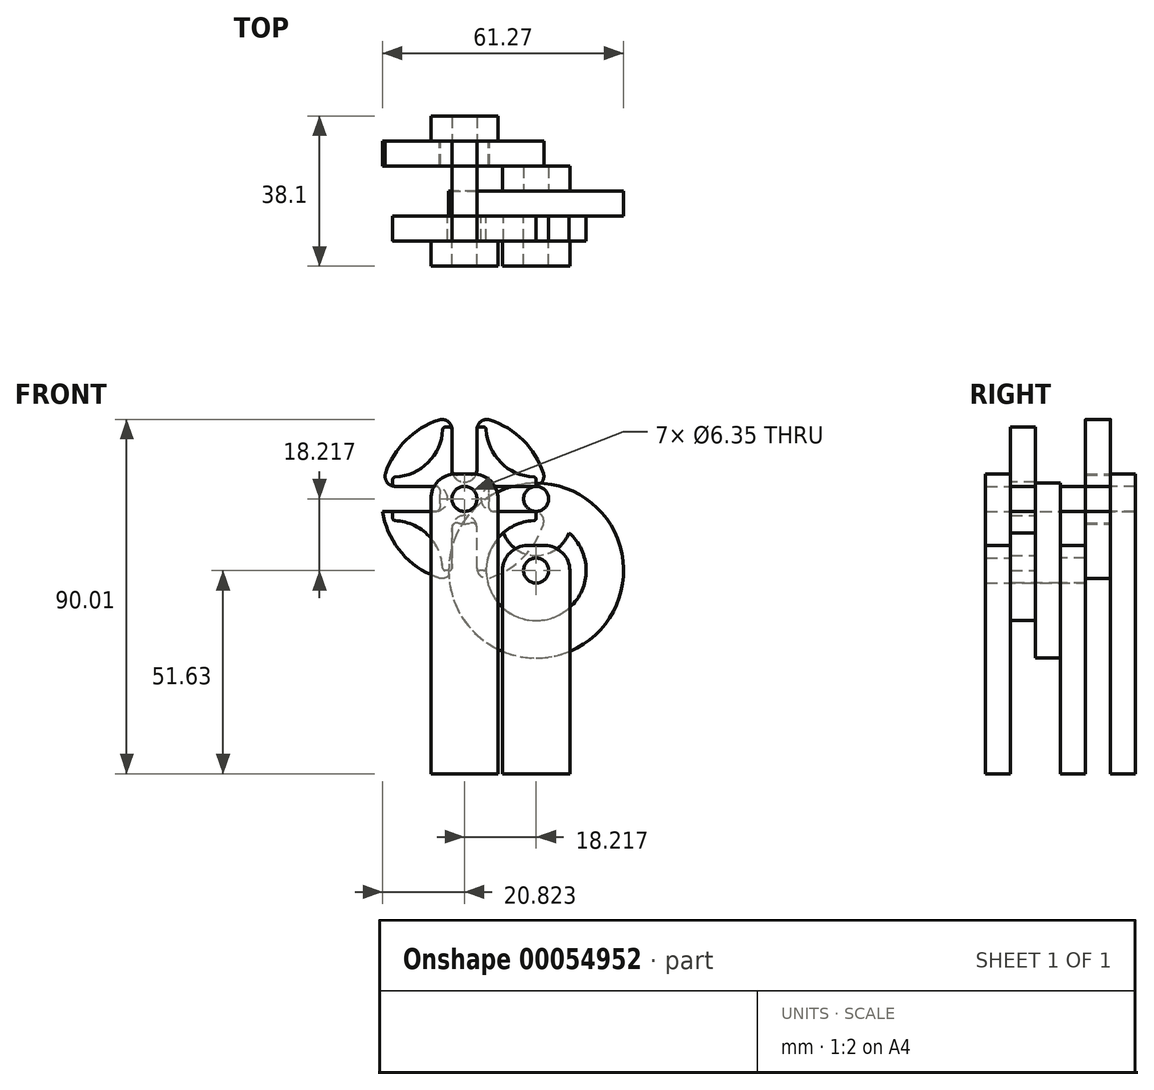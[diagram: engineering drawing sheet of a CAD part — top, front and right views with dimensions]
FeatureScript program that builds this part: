
annotation { "Feature Type Name" : "Feature", "Feature Type Description" : "" }
export const myFeature = defineFeature(function(context is Context, id is Id, definition is map)
    precondition{}
    {
        {
            var Q0;
            Q0=qCreatedBy(makeId("Front.planeOp"),FACE);
            var sketch = newSketch(context, id + "F0", { "sketchPlane" : qUnion([Q0])});
            skCircle(sketch, "E0", {"center": v(0, 0) * mm, "radius": 12.7 * mm});
            skCircle(sketch, "E1", {"center": v(0, 0) * mm, "radius": 22.23 * mm});
            skArc(sketch, "E2", {"start": v(-8.33, 9.59) * mm, "mid": v(0, 3.81) * mm, "end": v(8.33, 9.59) * mm});
            skCircle(sketch, "E3", {"center": v(0, 18.22) * mm, "radius": 3.18 * mm});
            skCircle(sketch, "E4", {"center": v(0, 0) * mm, "radius": 3.18 * mm});
            skSolve(sketch);
        }
        {
            var Q0;
            Q0=makeQuery(id+"F0.imprint","IMPRINT",FACE,{"disambiguationData":[TD([[makeQuery(id+"F0.imprint","IMPRINT",EDGE,{"derivedFrom":sQuery(id+"F0.wireOp",EDGE,"E1")}),1.0]])]});
            var Q1;
            Q1=makeQuery(id+"F0.imprint","IMPRINT",FACE,{"disambiguationData":[TD([[makeQuery(id+"F0.imprint","IMPRINT",EDGE,{"derivedFrom":sQuery(id+"F0.wireOp",EDGE,"E3")}),1.0]])]});
            var Q2;
            {var subQ0=sQuery(id+"F0.wireOp",EDGE,"E2");Q2=makeQuery(id+"F0.imprint","IMPRINT",FACE,{"disambiguationData":[TD([[makeQuery(id+"F0.imprint","IMPRINT",EDGE,{"derivedFrom":subQ0}),1.0]])]});}
            var Q3;
            {var subQ0=sQuery(id+"F0.wireOp",EDGE,"E2");Q3=makeQuery(id+"F0.imprint","IMPRINT",FACE,{"disambiguationData":[TD([[makeQuery(id+"F0.imprint","IMPRINT",EDGE,{"derivedFrom":subQ0}),-1.0]])]});}
            extrude(context, id + "F1", {"entities" : qUnion([Q0, Q1, Q2, Q3]), "oppositeDirection" : true, "depth" : 6.35 * mm});
        }
        {
            var Q0;
            Q0=makeQuery(id+"F0.imprint","IMPRINT",FACE,{"disambiguationData":[TD([[makeQuery(id+"F0.imprint","IMPRINT",EDGE,{"derivedFrom":sQuery(id+"F0.wireOp",EDGE,"E3")}),1.0]])]});
            var Q1;
            {var subQ0=sQuery(id+"F0.wireOp",EDGE,"E2");Q1=makeQuery(id+"F0.imprint","IMPRINT",FACE,{"disambiguationData":[TD([[makeQuery(id+"F0.imprint","IMPRINT",EDGE,{"derivedFrom":subQ0}),-1.0]])]});}
            extrude(context, id + "F2", {"entities" : qUnion([Q0, Q1]), "operationType" : NewBodyOperationType.ADD, "depth" : 6.35 * mm});
        }
        {
            var Q0;
            Q0=makeQuery(id+"F1.opExtrude","CAP_FACE",FACE,{"disambiguationData":[OSD([sQuery(id+"F0.wireOp",EDGE,"E1")])],"isStart":true});
            var sketch = newSketch(context, id + "F3", { "sketchPlane" : qUnion([Q0])});
            skArc(sketch, "E5", {"start": v(-12.7, 0) * mm, "mid": v(-8.98, 8.98) * mm, "end": v(0, 12.7) * mm});
            skLineSegment(sketch, "E6.bottom", {"start": v(0, 0) * mm, "end": v(-36.43, 0) * mm});
            skLineSegment(sketch, "E6.top", {"start": v(0, 36.43) * mm, "end": v(-36.43, 36.43) * mm});
            skLineSegment(sketch, "E6.left", {"start": v(0, 0) * mm, "end": v(0, 36.43) * mm});
            skLineSegment(sketch, "E6.right", {"start": v(-36.43, 0) * mm, "end": v(-36.43, 36.43) * mm});
            skLineSegment(sketch, "E7", {"start": v(-18.22, 36.43) * mm, "end": v(-18.22, 0) * mm, "construction": true});
            skLineSegment(sketch, "E8", {"start": v(-36.43, 18.22) * mm, "end": v(0, 18.22) * mm, "construction": true});
            skPoint(sketch, "E9", {"position": v(-18.22, 18.22) * mm});
            skCircle(sketch, "E10", {"center": v(-18.22, 18.22) * mm, "radius": 3.18 * mm});
            skLineSegment(sketch, "E11.bottom", {"start": v(0, 21.4) * mm, "end": v(-13.97, 21.4) * mm});
            skLineSegment(sketch, "E11.top", {"start": v(0, 15.04) * mm, "end": v(-13.97, 15.04) * mm});
            skLineSegment(sketch, "E11.left", {"start": v(0, 15.04) * mm, "end": v(0, 21.4) * mm});
            skLineSegment(sketch, "E11.right", {"start": v(-13.97, 15.04) * mm, "end": v(-13.97, 21.4) * mm});
            skLineSegment(sketch, "E12.1.0", {"start": v(-15.04, 36.43) * mm, "end": v(-15.04, 22.46) * mm});
            skLineSegment(sketch, "E12.1.1", {"start": v(-15.04, 22.46) * mm, "end": v(-21.4, 22.46) * mm});
            skLineSegment(sketch, "E12.1.2", {"start": v(-21.4, 36.43) * mm, "end": v(-21.4, 22.46) * mm});
            skArc(sketch, "E12.1.3", {"start": v(0, 23.73) * mm, "mid": v(-8.98, 27.45) * mm, "end": v(-12.7, 36.43) * mm});
            skLineSegment(sketch, "E12.2.0", {"start": v(-36.43, 21.4) * mm, "end": v(-22.46, 21.4) * mm});
            skLineSegment(sketch, "E12.2.1", {"start": v(-22.46, 21.4) * mm, "end": v(-22.46, 15.04) * mm});
            skLineSegment(sketch, "E12.2.2", {"start": v(-36.43, 15.04) * mm, "end": v(-22.46, 15.04) * mm});
            skArc(sketch, "E12.2.3", {"start": v(-23.73, 36.43) * mm, "mid": v(-27.45, 27.45) * mm, "end": v(-36.43, 23.73) * mm});
            skLineSegment(sketch, "E12.3.0", {"start": v(-21.4, 0) * mm, "end": v(-21.4, 13.97) * mm});
            skLineSegment(sketch, "E12.3.1", {"start": v(-21.4, 13.97) * mm, "end": v(-15.04, 13.97) * mm});
            skLineSegment(sketch, "E12.3.2", {"start": v(-15.04, 0) * mm, "end": v(-15.04, 13.97) * mm});
            skArc(sketch, "E12.3.3", {"start": v(-36.43, 12.7) * mm, "mid": v(-27.45, 8.98) * mm, "end": v(-23.73, 0) * mm});
            skLineSegment(sketch, "E13", {"start": v(0, 21.4) * mm, "end": v(0, 15.04) * mm});
            skLineSegment(sketch, "E14", {"start": v(-15.04, 36.43) * mm, "end": v(-21.4, 36.43) * mm});
            skLineSegment(sketch, "E15", {"start": v(-36.43, 21.4) * mm, "end": v(-36.43, 15.04) * mm});
            skLineSegment(sketch, "E16", {"start": v(-21.4, 0) * mm, "end": v(-15.04, 0) * mm});
            skSolve(sketch);
        }
        {
            var Q0;
            {var subQ5=sQuery(id+"F3.wireOp",EDGE,"E11.top");Q0=makeQuery(id+"F3.imprint","IMPRINT",FACE,{"disambiguationData":[TD([[makeQuery(id+"F3.imprint","IMPRINT",EDGE,{"derivedFrom":subQ5}),1.0]])]});}
            var Q1;
            {var subQ2=sQuery(id+"F3.wireOp",EDGE,"E12.1.0");Q1=makeQuery(id+"F3.imprint","IMPRINT",FACE,{"disambiguationData":[TD([[makeQuery(id+"F3.imprint","IMPRINT",EDGE,{"derivedFrom":subQ2}),1.0]])]});}
            var Q2;
            {var subQ0=sQuery(id+"F3.wireOp",EDGE,"E11.bottom");var subQ3=makeQuery(id+"F1.opExtrude","CAP_EDGE",EDGE,{"disambiguationData":[OSD([sQuery(id+"F0.wireOp",EDGE,"E1")])],"isStart":true});var subQ5=makeQuery(id+"F3.imprint","INTERSECT",VERTEX,{"derivedFrom":[subQ3,subQ0]});Q2=makeQuery(id+"F3.imprint","IMPRINT",FACE,{"disambiguationData":[TD([[makeQuery(id+"F3.imprint","IMPRINT",EDGE,{"disambiguationData":[TD([[subQ5,1.0]])],"derivedFrom":subQ3}),1.0]])]});}
            var Q3;
            {var subQ0=sQuery(id+"F3.wireOp",EDGE,"E12.3.0");var subQ3=makeQuery(id+"F1.opExtrude","CAP_EDGE",EDGE,{"disambiguationData":[OSD([sQuery(id+"F0.wireOp",EDGE,"E1")])],"isStart":true});var subQ5=makeQuery(id+"F3.imprint","INTERSECT",VERTEX,{"derivedFrom":[subQ3,subQ0]});Q3=makeQuery(id+"F3.imprint","IMPRINT",FACE,{"disambiguationData":[TD([[makeQuery(id+"F3.imprint","IMPRINT",EDGE,{"disambiguationData":[TD([[subQ5,1.0]])],"derivedFrom":subQ0}),1.0]])]});}
            extrude(context, id + "F4", {"entities" : qUnion([Q0, Q1, Q2, Q3]), "depth" : 6.35 * mm});
        }
        {
            var Q0;
            Q0=makeQuery(id+"F0.imprint","IMPRINT",FACE,{"disambiguationData":[TD([[makeQuery(id+"F0.imprint","IMPRINT",EDGE,{"derivedFrom":sQuery(id+"F0.wireOp",EDGE,"E4")}),1.0]])]});
            extrude(context, id + "F5", {"entities" : qUnion([Q0]), "depth" : 12.7 * mm, "hasSecondDirection" : true, "secondDirectionOppositeDirection" : true, "secondDirectionDepth" : 12.7 * mm});
        }
        {
            var Q0;
            Q0=makeQuery(id+"F3.imprint","IMPRINT",FACE,{"disambiguationData":[TD([[makeQuery(id+"F3.imprint","IMPRINT",EDGE,{"derivedFrom":sQuery(id+"F3.wireOp",EDGE,"E10")}),1.0]])]});
            var Q1;
            Q1=makeQuery(id+"F5.opExtrude","CAP_FACE",FACE,{"disambiguationData":[OSD([sQuery(id+"F0.wireOp",EDGE,"E4")])],"isStart":false});
            extrude(context, id + "F6", {"entities" : qUnion([Q0]), "endBoundEntityFace" : qUnion([Q1]), "depth" : 12.7 * mm, "hasSecondDirection" : true, "secondDirectionOppositeDirection" : true, "secondDirectionDepth" : 25.4 * mm});
        }
        {
            var Q0;
            Q0=makeQuery(id+"F4.opExtrude","SWEPT_EDGE",EDGE,{"disambiguationData":[OSD([sQuery(id+"F3.wireOp",EDGE,"E12.1.0"),sQuery(id+"F3.wireOp",EDGE,"E12.1.1")])]});
            var Q1;
            Q1=makeQuery(id+"F4.opExtrude","SWEPT_EDGE",EDGE,{"disambiguationData":[OSD([sQuery(id+"F3.wireOp",EDGE,"E12.1.1"),sQuery(id+"F3.wireOp",EDGE,"E12.1.2")])]});
            var Q2;
            Q2=makeQuery(id+"F4.opExtrude","SWEPT_EDGE",EDGE,{"disambiguationData":[OSD([sQuery(id+"F3.wireOp",EDGE,"E11.bottom"),sQuery(id+"F3.wireOp",EDGE,"E11.right")])]});
            var Q3;
            Q3=makeQuery(id+"F4.opExtrude","SWEPT_EDGE",EDGE,{"disambiguationData":[OSD([sQuery(id+"F3.wireOp",EDGE,"E11.top"),sQuery(id+"F3.wireOp",EDGE,"E11.right")])]});
            var Q4;
            Q4=makeQuery(id+"F4.opExtrude","SWEPT_EDGE",EDGE,{"disambiguationData":[OSD([sQuery(id+"F3.wireOp",EDGE,"E12.3.1"),sQuery(id+"F3.wireOp",EDGE,"E12.3.2")])]});
            var Q5;
            Q5=makeQuery(id+"F4.opExtrude","SWEPT_EDGE",EDGE,{"disambiguationData":[OSD([sQuery(id+"F3.wireOp",EDGE,"E12.3.0"),sQuery(id+"F3.wireOp",EDGE,"E12.3.1")])]});
            var Q6;
            Q6=makeQuery(id+"F4.opExtrude","SWEPT_EDGE",EDGE,{"disambiguationData":[OSD([sQuery(id+"F3.wireOp",EDGE,"E12.2.1"),sQuery(id+"F3.wireOp",EDGE,"E12.2.2")])]});
            var Q7;
            Q7=makeQuery(id+"F4.opExtrude","SWEPT_EDGE",EDGE,{"disambiguationData":[OSD([sQuery(id+"F3.wireOp",EDGE,"E12.2.0"),sQuery(id+"F3.wireOp",EDGE,"E12.2.1")])]});
            fillet(context, id + "F7", {"entities" : qUnion([Q0, Q1, Q2, Q3, Q4, Q5, Q6, Q7]), "radius" : 3.17 * mm, "tangentPropagation" : true, "allowEdgeOverflow" : false});
        }
        {
            var Q0;
            Q0=makeQuery(id+"F4.opExtrude","SWEPT_EDGE",EDGE,{"disambiguationData":[OSD([sQuery(id+"F3.wireOp",EDGE,"E6.top"),sQuery(id+"F3.wireOp",EDGE,"E12.1.3")])]});
            var Q1;
            Q1=makeQuery(id+"F4.opExtrude","SWEPT_EDGE",EDGE,{"disambiguationData":[OSD([sQuery(id+"F3.wireOp",EDGE,"E6.top"),sQuery(id+"F3.wireOp",EDGE,"E12.1.0"),sQuery(id+"F3.wireOp",EDGE,"E14")])]});
            var Q2;
            Q2=makeQuery(id+"F4.opExtrude","SWEPT_EDGE",EDGE,{"disambiguationData":[OSD([sQuery(id+"F3.wireOp",EDGE,"E6.top"),sQuery(id+"F3.wireOp",EDGE,"E12.1.2"),sQuery(id+"F3.wireOp",EDGE,"E14")])]});
            var Q3;
            Q3=makeQuery(id+"F4.opExtrude","SWEPT_EDGE",EDGE,{"disambiguationData":[OSD([sQuery(id+"F3.wireOp",EDGE,"E6.top"),sQuery(id+"F3.wireOp",EDGE,"E12.2.3")])]});
            var Q4;
            Q4=makeQuery(id+"F4.opExtrude","SWEPT_EDGE",EDGE,{"disambiguationData":[OSD([sQuery(id+"F3.wireOp",EDGE,"E6.right"),sQuery(id+"F3.wireOp",EDGE,"E12.2.3")])]});
            var Q5;
            Q5=makeQuery(id+"F4.opExtrude","SWEPT_EDGE",EDGE,{"disambiguationData":[OSD([sQuery(id+"F3.wireOp",EDGE,"E6.left"),sQuery(id+"F3.wireOp",EDGE,"E12.1.3")])]});
            var Q6;
            Q6=makeQuery(id+"F4.opExtrude","SWEPT_EDGE",EDGE,{"disambiguationData":[OSD([sQuery(id+"F0.wireOp",EDGE,"E3"),sQuery(id+"F3.wireOp",EDGE,"E6.left"),sQuery(id+"F3.wireOp",EDGE,"E11.bottom"),sQuery(id+"F3.wireOp",EDGE,"E13")])]});
            var Q7;
            Q7=makeQuery(id+"F4.opExtrude","SWEPT_EDGE",EDGE,{"disambiguationData":[OSD([sQuery(id+"F3.wireOp",EDGE,"E5"),sQuery(id+"F3.wireOp",EDGE,"E6.left")])]});
            var Q8;
            Q8=makeQuery(id+"F4.opExtrude","SWEPT_EDGE",EDGE,{"disambiguationData":[OSD([sQuery(id+"F3.wireOp",EDGE,"E6.right"),sQuery(id+"F3.wireOp",EDGE,"E12.2.2"),sQuery(id+"F3.wireOp",EDGE,"E15")])]});
            var Q9;
            Q9=makeQuery(id+"F4.opExtrude","SWEPT_EDGE",EDGE,{"disambiguationData":[OSD([sQuery(id+"F3.wireOp",EDGE,"E6.bottom"),sQuery(id+"F3.wireOp",EDGE,"E12.3.0"),sQuery(id+"F3.wireOp",EDGE,"E16")])]});
            var Q10;
            Q10=makeQuery(id+"F4.opExtrude","SWEPT_EDGE",EDGE,{"disambiguationData":[OSD([sQuery(id+"F3.wireOp",EDGE,"E6.right"),sQuery(id+"F3.wireOp",EDGE,"E12.2.0"),sQuery(id+"F3.wireOp",EDGE,"E15")])]});
            var Q11;
            Q11=makeQuery(id+"F4.opExtrude","SWEPT_EDGE",EDGE,{"disambiguationData":[OSD([sQuery(id+"F3.wireOp",EDGE,"E6.right"),sQuery(id+"F3.wireOp",EDGE,"E12.3.3")])]});
            var Q12;
            Q12=makeQuery(id+"F4.opExtrude","SWEPT_EDGE",EDGE,{"disambiguationData":[OSD([sQuery(id+"F3.wireOp",EDGE,"E6.bottom"),sQuery(id+"F3.wireOp",EDGE,"E12.3.3")])]});
            var Q13;
            Q13=makeQuery(id+"F4.opExtrude","SWEPT_EDGE",EDGE,{"disambiguationData":[OSD([sQuery(id+"F3.wireOp",EDGE,"E6.bottom"),sQuery(id+"F3.wireOp",EDGE,"E12.3.2"),sQuery(id+"F3.wireOp",EDGE,"E16")])]});
            var Q14;
            Q14=makeQuery(id+"F4.opExtrude","SWEPT_EDGE",EDGE,{"disambiguationData":[OSD([sQuery(id+"F0.wireOp",EDGE,"E0"),sQuery(id+"F3.wireOp",EDGE,"E5"),sQuery(id+"F3.wireOp",EDGE,"E6.bottom")])]});
            var Q15;
            Q15=makeQuery(id+"F4.opExtrude","SWEPT_EDGE",EDGE,{"disambiguationData":[OSD([sQuery(id+"F0.wireOp",EDGE,"E3"),sQuery(id+"F3.wireOp",EDGE,"E6.left"),sQuery(id+"F3.wireOp",EDGE,"E11.top"),sQuery(id+"F3.wireOp",EDGE,"E13")])]});
            fillet(context, id + "F8", {"entities" : qUnion([Q0, Q1, Q2, Q3, Q4, Q5, Q6, Q7, Q8, Q9, Q10, Q11, Q12, Q13, Q14, Q15]), "radius" : 0.64 * mm, "tangentPropagation" : true, "allowEdgeOverflow" : false});
        }
        {
            var Q0;
            Q0=makeQuery(id+"F2.opExtrude","CAP_FACE",FACE,{"disambiguationData":[OSD([sQuery(id+"F0.wireOp",EDGE,"E0"),sQuery(id+"F0.wireOp",EDGE,"E2"),sQuery(id+"F0.wireOp",EDGE,"E4")])],"isStart":false});
            var sketch = newSketch(context, id + "F9", { "sketchPlane" : qUnion([Q0])});
            skLineSegment(sketch, "E17.bottom", {"start": v(-8.55, 6.35) * mm, "end": v(8.55, 6.35) * mm});
            skLineSegment(sketch, "E17.left", {"start": v(-8.55, 6.35) * mm, "end": v(-8.55, -51.63) * mm});
            skLineSegment(sketch, "E17.right", {"start": v(8.55, 6.35) * mm, "end": v(8.55, -51.63) * mm});
            skLineSegment(sketch, "E18", {"start": v(0, -51.63) * mm, "end": v(0, 6.35) * mm, "construction": true});
            skCircle(sketch, "E19", {"center": v(0, 0) * mm, "radius": 3.18 * mm});
            skLineSegment(sketch, "E20", {"start": v(-8.55, -51.63) * mm, "end": v(8.55, -51.63) * mm});
            skLineSegment(sketch, "E21.bottom", {"start": v(-26.76, 24.57) * mm, "end": v(-9.67, 24.57) * mm});
            skLineSegment(sketch, "E21.top", {"start": v(-26.76, -51.63) * mm, "end": v(-9.67, -51.63) * mm});
            skLineSegment(sketch, "E21.left", {"start": v(-26.76, 24.57) * mm, "end": v(-26.76, -51.63) * mm});
            skLineSegment(sketch, "E21.right", {"start": v(-9.67, 24.57) * mm, "end": v(-9.67, -51.63) * mm});
            skLineSegment(sketch, "E22", {"start": v(-18.22, 24.57) * mm, "end": v(-18.22, -51.63) * mm, "construction": true});
            skCircle(sketch, "E23.0", {"center": v(-18.22, 18.22) * mm, "radius": 3.18 * mm});
            skSolve(sketch);
        }
        {
            var Q0;
            Q0 = qSketchRegion(id + "F9", true);
            extrude(context, id + "F10", {"entities" : qUnion([Q0]), "depth" : 6.35 * mm});
        }
        {
            var Q0;
            Q0=makeQuery(id+"F1.opExtrude","CAP_FACE",FACE,{"disambiguationData":[OSD([sQuery(id+"F0.wireOp",EDGE,"E1"),sQuery(id+"F0.wireOp",EDGE,"E4")])],"isStart":false});
            var sketch = newSketch(context, id + "F11", { "sketchPlane" : qUnion([Q0])});
            skLineSegment(sketch, "E24.0.0", {"start": v(8.55, 6.35) * mm, "end": v(-8.55, 6.35) * mm});
            skLineSegment(sketch, "E24.0.1", {"start": v(-8.55, 6.35) * mm, "end": v(-8.55, -51.63) * mm});
            skLineSegment(sketch, "E24.0.2", {"start": v(-8.55, -51.63) * mm, "end": v(8.55, -51.63) * mm});
            skLineSegment(sketch, "E24.0.3", {"start": v(8.55, -51.63) * mm, "end": v(8.55, 6.35) * mm});
            skCircle(sketch, "E25.0", {"center": v(0, 0) * mm, "radius": 3.18 * mm});
            skSolve(sketch);
        }
        {
            var Q0;
            Q0 = qSketchRegion(id + "F11", true);
            extrude(context, id + "F12", {"entities" : qUnion([Q0]), "depth" : 6.35 * mm});
        }
        {
            var Q0;
            Q0=makeQuery(id+"F12.opExtrude","CAP_FACE",FACE,{"disambiguationData":[OSD([sQuery(id+"F11.wireOp",EDGE,"E24.0.0"),sQuery(id+"F11.wireOp",EDGE,"E24.0.1"),sQuery(id+"F11.wireOp",EDGE,"E24.0.2"),sQuery(id+"F11.wireOp",EDGE,"E24.0.3"),sQuery(id+"F11.wireOp",EDGE,"E25.0")])],"isStart":false});
            var sketch = newSketch(context, id + "F13", { "sketchPlane" : qUnion([Q0])});
            skCircle(sketch, "E26.0", {"center": v(18.22, 18.22) * mm, "radius": 3.18 * mm});
            skCircle(sketch, "E27", {"center": v(18.22, 18.22) * mm, "radius": 27.42 * mm});
            skLineSegment(sketch, "E28.bottom", {"start": v(11.87, 44.89) * mm, "end": v(24.57, 44.89) * mm});
            skLineSegment(sketch, "E28.top", {"start": v(11.87, 33.08) * mm, "end": v(24.57, 33.08) * mm});
            skLineSegment(sketch, "E28.left", {"start": v(11.87, 44.89) * mm, "end": v(11.87, 33.08) * mm});
            skLineSegment(sketch, "E28.right", {"start": v(24.57, 44.89) * mm, "end": v(24.57, 33.08) * mm});
            skLineSegment(sketch, "E29.1.0", {"start": v(-8.45, 11.87) * mm, "end": v(-8.45, 24.57) * mm});
            skLineSegment(sketch, "E29.1.1", {"start": v(-8.45, 24.57) * mm, "end": v(3.35, 24.57) * mm});
            skLineSegment(sketch, "E29.1.2", {"start": v(-8.45, 11.87) * mm, "end": v(3.35, 11.87) * mm});
            skLineSegment(sketch, "E29.1.3", {"start": v(3.35, 11.87) * mm, "end": v(3.35, 24.57) * mm});
            skLineSegment(sketch, "E29.2.0", {"start": v(24.57, -8.45) * mm, "end": v(11.87, -8.45) * mm});
            skLineSegment(sketch, "E29.2.1", {"start": v(11.87, -8.45) * mm, "end": v(11.87, 3.35) * mm});
            skLineSegment(sketch, "E29.2.2", {"start": v(24.57, -8.45) * mm, "end": v(24.57, 3.35) * mm});
            skLineSegment(sketch, "E29.2.3", {"start": v(24.57, 3.35) * mm, "end": v(11.87, 3.35) * mm});
            skLineSegment(sketch, "E29.3.0", {"start": v(44.89, 24.57) * mm, "end": v(44.89, 11.87) * mm});
            skLineSegment(sketch, "E29.3.1", {"start": v(44.89, 11.87) * mm, "end": v(33.08, 11.87) * mm});
            skLineSegment(sketch, "E29.3.2", {"start": v(44.89, 24.57) * mm, "end": v(33.08, 24.57) * mm});
            skLineSegment(sketch, "E29.3.3", {"start": v(33.08, 24.57) * mm, "end": v(33.08, 11.87) * mm});
            skPoint(sketch, "E30", {"position": v(18.22, 33.08) * mm});
            skLineSegment(sketch, "E31.bottom", {"start": v(-5.28, 75.37) * mm, "end": v(41.71, 75.37) * mm});
            skLineSegment(sketch, "E31.top", {"start": v(-5.28, 44.89) * mm, "end": v(41.71, 44.89) * mm});
            skLineSegment(sketch, "E31.left", {"start": v(-8.45, 72.2) * mm, "end": v(-8.45, 48.06) * mm});
            skLineSegment(sketch, "E31.right", {"start": v(44.89, 72.2) * mm, "end": v(44.89, 48.06) * mm});
            skPoint(sketch, "E32", {"position": v(18.22, 44.89) * mm});
            skPoint(sketch, "E33.visualSharp", {"position": v(-8.45, 75.37) * mm});
            skArc(sketch, "E33.filletArc", {"start": v(-5.28, 75.37) * mm, "mid": v(-7.52, 74.44) * mm, "end": v(-8.45, 72.2) * mm});
            skPoint(sketch, "E34.visualSharp", {"position": v(44.89, 75.37) * mm});
            skArc(sketch, "E34.filletArc", {"start": v(44.89, 72.2) * mm, "mid": v(43.96, 74.44) * mm, "end": v(41.71, 75.37) * mm});
            skPoint(sketch, "E35.visualSharp", {"position": v(44.89, 44.89) * mm});
            skArc(sketch, "E35.filletArc", {"start": v(41.71, 44.89) * mm, "mid": v(43.96, 45.82) * mm, "end": v(44.89, 48.06) * mm});
            skPoint(sketch, "E36.visualSharp", {"position": v(-8.45, 44.89) * mm});
            skArc(sketch, "E36.filletArc", {"start": v(-8.45, 48.06) * mm, "mid": v(-7.52, 45.82) * mm, "end": v(-5.28, 44.89) * mm});
            skLineSegment(sketch, "E37.1.0", {"start": v(-35.76, 44.89) * mm, "end": v(-11.63, 44.89) * mm});
            skPoint(sketch, "E37.1.1", {"position": v(-8.45, 18.22) * mm});
            skLineSegment(sketch, "E37.1.2", {"start": v(-35.76, -8.45) * mm, "end": v(-11.63, -8.45) * mm});
            skPoint(sketch, "E37.1.3", {"position": v(-8.45, -8.45) * mm});
            skPoint(sketch, "E37.1.5", {"position": v(-38.93, 44.89) * mm});
            skPoint(sketch, "E37.1.6", {"position": v(-38.93, -8.45) * mm});
            skLineSegment(sketch, "E37.1.7", {"start": v(-38.93, -5.28) * mm, "end": v(-38.93, 41.71) * mm});
            skLineSegment(sketch, "E37.1.8", {"start": v(-8.45, -5.28) * mm, "end": v(-8.45, 41.71) * mm});
            skArc(sketch, "E37.1.10", {"start": v(-35.76, 44.89) * mm, "mid": v(-38, 43.96) * mm, "end": v(-38.93, 41.71) * mm});
            skArc(sketch, "E37.1.11", {"start": v(-8.45, 41.71) * mm, "mid": v(-9.38, 43.96) * mm, "end": v(-11.63, 44.89) * mm});
            skArc(sketch, "E37.1.12", {"start": v(-38.93, -5.28) * mm, "mid": v(-38, -7.52) * mm, "end": v(-35.76, -8.45) * mm});
            skArc(sketch, "E37.1.13", {"start": v(-11.63, -8.45) * mm, "mid": v(-9.38, -7.52) * mm, "end": v(-8.45, -5.28) * mm});
            skLineSegment(sketch, "E37.2.0", {"start": v(-8.45, -35.76) * mm, "end": v(-8.45, -11.63) * mm});
            skPoint(sketch, "E37.2.1", {"position": v(18.22, -8.45) * mm});
            skLineSegment(sketch, "E37.2.2", {"start": v(44.89, -35.76) * mm, "end": v(44.89, -11.63) * mm});
            skPoint(sketch, "E37.2.3", {"position": v(44.89, -8.45) * mm});
            skPoint(sketch, "E37.2.4", {"position": v(-8.45, -8.45) * mm});
            skPoint(sketch, "E37.2.5", {"position": v(-8.45, -38.93) * mm});
            skPoint(sketch, "E37.2.6", {"position": v(44.89, -38.93) * mm});
            skLineSegment(sketch, "E37.2.7", {"start": v(41.71, -38.93) * mm, "end": v(-5.28, -38.93) * mm});
            skLineSegment(sketch, "E37.2.8", {"start": v(41.71, -8.45) * mm, "end": v(-5.28, -8.45) * mm});
            skArc(sketch, "E37.2.10", {"start": v(-8.45, -35.76) * mm, "mid": v(-7.52, -38) * mm, "end": v(-5.28, -38.93) * mm});
            skArc(sketch, "E37.2.11", {"start": v(-5.28, -8.45) * mm, "mid": v(-7.52, -9.38) * mm, "end": v(-8.45, -11.63) * mm});
            skArc(sketch, "E37.2.12", {"start": v(41.71, -38.93) * mm, "mid": v(43.96, -38) * mm, "end": v(44.89, -35.76) * mm});
            skArc(sketch, "E37.2.13", {"start": v(44.89, -11.63) * mm, "mid": v(43.96, -9.38) * mm, "end": v(41.71, -8.45) * mm});
            skLineSegment(sketch, "E37.3.0", {"start": v(72.2, -8.45) * mm, "end": v(48.06, -8.45) * mm});
            skPoint(sketch, "E37.3.1", {"position": v(44.89, 18.22) * mm});
            skLineSegment(sketch, "E37.3.2", {"start": v(72.2, 44.89) * mm, "end": v(48.06, 44.89) * mm});
            skPoint(sketch, "E37.3.4", {"position": v(44.89, -8.45) * mm});
            skPoint(sketch, "E37.3.5", {"position": v(75.37, -8.45) * mm});
            skPoint(sketch, "E37.3.6", {"position": v(75.37, 44.89) * mm});
            skLineSegment(sketch, "E37.3.7", {"start": v(75.37, 41.71) * mm, "end": v(75.37, -5.28) * mm});
            skLineSegment(sketch, "E37.3.8", {"start": v(44.89, 41.71) * mm, "end": v(44.89, -5.28) * mm});
            skArc(sketch, "E37.3.10", {"start": v(72.2, -8.45) * mm, "mid": v(74.44, -7.52) * mm, "end": v(75.37, -5.28) * mm});
            skArc(sketch, "E37.3.11", {"start": v(44.89, -5.28) * mm, "mid": v(45.82, -7.52) * mm, "end": v(48.06, -8.45) * mm});
            skArc(sketch, "E37.3.12", {"start": v(75.37, 41.71) * mm, "mid": v(74.44, 43.96) * mm, "end": v(72.2, 44.89) * mm});
            skArc(sketch, "E37.3.13", {"start": v(48.06, 44.89) * mm, "mid": v(45.82, 43.96) * mm, "end": v(44.89, 41.71) * mm});
            skSolve(sketch);
        }
        {
            var Q0;
            Q0 = qSketchRegion(id + "F13", true);
            var Q1;
            {var subQ0=sQuery(id+"F13.wireOp",EDGE,"E28.top");var subQ1=sQuery(id+"F13.wireOp",EDGE,"E26.0");var subQ2=makeQuery(id+"F13.imprint","INTERSECT",VERTEX,{"derivedFrom":[subQ1,subQ0]});Q1=makeQuery(id+"F13.imprint","IMPRINT",FACE,{"disambiguationData":[TD([[makeQuery(id+"F13.imprint","IMPRINT",EDGE,{"disambiguationData":[TD([[subQ2,-1.0]])],"derivedFrom":subQ1}),-1.0]])]});}
            var Q2;
            {var subQ0=sQuery(id+"F13.wireOp",EDGE,"E28.top");var subQ1=sQuery(id+"F13.wireOp",EDGE,"E26.0");var subQ2=makeQuery(id+"F13.imprint","INTERSECT",VERTEX,{"derivedFrom":[subQ1,subQ0]});Q2=makeQuery(id+"F13.imprint","IMPRINT",FACE,{"disambiguationData":[TD([[makeQuery(id+"F13.imprint","IMPRINT",EDGE,{"disambiguationData":[TD([[subQ2,1.0]])],"derivedFrom":subQ1}),-1.0]])]});}
            var Q3;
            {var subQ0=sQuery(id+"F13.wireOp",EDGE,"E29.1.3");var subQ1=sQuery(id+"F13.wireOp",EDGE,"E26.0");var subQ2=makeQuery(id+"F13.imprint","INTERSECT",VERTEX,{"derivedFrom":[subQ1,subQ0]});Q3=makeQuery(id+"F13.imprint","IMPRINT",FACE,{"disambiguationData":[TD([[makeQuery(id+"F13.imprint","IMPRINT",EDGE,{"disambiguationData":[TD([[subQ2,-1.0]])],"derivedFrom":subQ1}),-1.0]])]});}
            var Q4;
            {var subQ0=sQuery(id+"F13.wireOp",EDGE,"E29.3.3");var subQ1=sQuery(id+"F13.wireOp",EDGE,"E26.0");var subQ2=makeQuery(id+"F13.imprint","INTERSECT",VERTEX,{"derivedFrom":[subQ1,subQ0]});Q4=makeQuery(id+"F13.imprint","IMPRINT",FACE,{"disambiguationData":[TD([[makeQuery(id+"F13.imprint","IMPRINT",EDGE,{"disambiguationData":[TD([[subQ2,1.0]])],"derivedFrom":subQ1}),-1.0]])]});}
            extrude(context, id + "F14", {"entities" : qUnion([Q0, Q1, Q2, Q3, Q4]), "depth" : 6.35 * mm});
        }
        {
            var Q0;
            Q0=makeQuery(id+"F14.opExtrude","CAP_FACE",FACE,{"disambiguationData":[OSD([sQuery(id+"F13.wireOp",EDGE,"E26.0"),sQuery(id+"F13.wireOp",EDGE,"E27"),sQuery(id+"F13.wireOp",EDGE,"E31.bottom"),sQuery(id+"F13.wireOp",EDGE,"E31.top"),sQuery(id+"F13.wireOp",EDGE,"E31.left"),sQuery(id+"F13.wireOp",EDGE,"E31.right"),sQuery(id+"F13.wireOp",EDGE,"E33.filletArc"),sQuery(id+"F13.wireOp",EDGE,"E34.filletArc"),sQuery(id+"F13.wireOp",EDGE,"E35.filletArc"),sQuery(id+"F13.wireOp",EDGE,"E36.filletArc"),sQuery(id+"F13.wireOp",EDGE,"E37.1.0"),sQuery(id+"F13.wireOp",EDGE,"E37.1.2"),sQuery(id+"F13.wireOp",EDGE,"E37.1.7"),sQuery(id+"F13.wireOp",EDGE,"E37.1.8"),sQuery(id+"F13.wireOp",EDGE,"E37.1.10"),sQuery(id+"F13.wireOp",EDGE,"E37.1.11"),sQuery(id+"F13.wireOp",EDGE,"E37.1.12"),sQuery(id+"F13.wireOp",EDGE,"E37.1.13"),sQuery(id+"F13.wireOp",EDGE,"E37.2.0"),sQuery(id+"F13.wireOp",EDGE,"E37.2.2"),sQuery(id+"F13.wireOp",EDGE,"E37.2.7"),sQuery(id+"F13.wireOp",EDGE,"E37.2.8"),sQuery(id+"F13.wireOp",EDGE,"E37.2.10"),sQuery(id+"F13.wireOp",EDGE,"E37.2.11"),sQuery(id+"F13.wireOp",EDGE,"E37.2.12"),sQuery(id+"F13.wireOp",EDGE,"E37.2.13"),sQuery(id+"F13.wireOp",EDGE,"E37.3.0"),sQuery(id+"F13.wireOp",EDGE,"E37.3.2"),sQuery(id+"F13.wireOp",EDGE,"E37.3.7"),sQuery(id+"F13.wireOp",EDGE,"E37.3.8"),sQuery(id+"F13.wireOp",EDGE,"E37.3.10"),sQuery(id+"F13.wireOp",EDGE,"E37.3.11"),sQuery(id+"F13.wireOp",EDGE,"E37.3.12"),sQuery(id+"F13.wireOp",EDGE,"E37.3.13")])],"isStart":false});
            var sketch = newSketch(context, id + "F15", { "sketchPlane" : qUnion([Q0])});
            skArc(sketch, "E38", {"start": v(21.4, 39.04) * mm, "mid": v(33.11, 33.11) * mm, "end": v(39.04, 21.4) * mm});
            skLineSegment(sketch, "E39", {"start": v(21.4, 39.04) * mm, "end": v(21.4, 21.4) * mm});
            skLineSegment(sketch, "E40", {"start": v(21.4, 21.4) * mm, "end": v(39.04, 21.4) * mm});
            skLineSegment(sketch, "E41.1.0", {"start": v(15.04, 21.4) * mm, "end": v(15.04, 39.04) * mm});
            skLineSegment(sketch, "E41.1.1", {"start": v(-2.6, 21.4) * mm, "end": v(15.04, 21.4) * mm});
            skArc(sketch, "E41.1.2", {"start": v(-2.6, 21.4) * mm, "mid": v(3.32, 33.11) * mm, "end": v(15.04, 39.04) * mm});
            skLineSegment(sketch, "E41.2.0", {"start": v(15.04, 15.04) * mm, "end": v(-2.6, 15.04) * mm});
            skLineSegment(sketch, "E41.2.1", {"start": v(15.04, -2.6) * mm, "end": v(15.04, 15.04) * mm});
            skArc(sketch, "E41.2.2", {"start": v(15.04, -2.6) * mm, "mid": v(3.32, 3.32) * mm, "end": v(-2.6, 15.04) * mm});
            skLineSegment(sketch, "E41.3.0", {"start": v(21.4, 15.04) * mm, "end": v(21.4, -2.6) * mm});
            skLineSegment(sketch, "E41.3.1", {"start": v(39.04, 15.04) * mm, "end": v(21.4, 15.04) * mm});
            skArc(sketch, "E41.3.2", {"start": v(39.04, 15.04) * mm, "mid": v(33.11, 3.32) * mm, "end": v(21.4, -2.6) * mm});
            skCircle(sketch, "E42", {"center": v(18.22, 18.22) * mm, "radius": 6.35 * mm});
            skSolve(sketch);
        }
        {
            var Q0;
            Q0=makeQuery(id+"F15.imprint","IMPRINT",FACE,{"disambiguationData":[TD([[makeQuery(id+"F15.imprint","IMPRINT",EDGE,{"derivedFrom":sQuery(id+"F15.wireOp",EDGE,"E38")}),-1.0]])]});
            var Q1;
            {var subQ0=sQuery(id+"F15.wireOp",EDGE,"E41.3.2");Q1=makeQuery(id+"F15.imprint","IMPRINT",FACE,{"disambiguationData":[TD([[makeQuery(id+"F15.imprint","IMPRINT",EDGE,{"derivedFrom":subQ0}),-1.0]])]});}
            var Q2;
            {var subQ0=sQuery(id+"F15.wireOp",EDGE,"E41.2.2");Q2=makeQuery(id+"F15.imprint","IMPRINT",FACE,{"disambiguationData":[TD([[makeQuery(id+"F15.imprint","IMPRINT",EDGE,{"derivedFrom":subQ0}),-1.0]])]});}
            var Q3;
            {var subQ0=sQuery(id+"F15.wireOp",EDGE,"E41.1.2");Q3=makeQuery(id+"F15.imprint","IMPRINT",FACE,{"disambiguationData":[TD([[makeQuery(id+"F15.imprint","IMPRINT",EDGE,{"derivedFrom":subQ0}),-1.0]])]});}
            extrude(context, id + "F16", {"entities" : qUnion([Q0, Q1, Q2, Q3]), "operationType" : NewBodyOperationType.REMOVE, "endBound" : BoundingType.UP_TO_NEXT, "oppositeDirection" : true, "depth" : 25.4 * mm});
        }
        {
            var Q0;
            Q0=makeQuery(id+"F14.opExtrude","SWEPT_EDGE",EDGE,{"disambiguationData":[OSD([sQuery(id+"F13.wireOp",EDGE,"E28.left"),sQuery(id+"F13.wireOp",EDGE,"E31.top")])]});
            var Q1;
            Q1=makeQuery(id+"F14.opExtrude","SWEPT_EDGE",EDGE,{"disambiguationData":[OSD([sQuery(id+"F13.wireOp",EDGE,"E28.right"),sQuery(id+"F13.wireOp",EDGE,"E31.top")])]});
            var Q2;
            Q2=makeQuery(id+"F14.opExtrude","SWEPT_EDGE",EDGE,{"disambiguationData":[OSD([sQuery(id+"F13.wireOp",EDGE,"E27"),sQuery(id+"F13.wireOp",EDGE,"E28.right")])]});
            var Q3;
            Q3=makeQuery(id+"F14.opExtrude","SWEPT_EDGE",EDGE,{"disambiguationData":[OSD([sQuery(id+"F13.wireOp",EDGE,"E27"),sQuery(id+"F13.wireOp",EDGE,"E28.left")])]});
            var Q4;
            Q4=makeQuery(id+"F14.opExtrude","SWEPT_EDGE",EDGE,{"disambiguationData":[OSD([sQuery(id+"F13.wireOp",EDGE,"E29.3.2"),sQuery(id+"F13.wireOp",EDGE,"E37.3.8"),sQuery(id+"F13.wireOp",EDGE,"E29.3.0")])]});
            var Q5;
            Q5=makeQuery(id+"F14.opExtrude","SWEPT_EDGE",EDGE,{"disambiguationData":[OSD([sQuery(id+"F13.wireOp",EDGE,"E27"),sQuery(id+"F13.wireOp",EDGE,"E29.3.2")])]});
            var Q6;
            Q6=makeQuery(id+"F14.opExtrude","SWEPT_EDGE",EDGE,{"disambiguationData":[OSD([sQuery(id+"F13.wireOp",EDGE,"E29.1.1"),sQuery(id+"F13.wireOp",EDGE,"E37.1.8"),sQuery(id+"F13.wireOp",EDGE,"E29.1.0")])]});
            var Q7;
            Q7=makeQuery(id+"F14.opExtrude","SWEPT_EDGE",EDGE,{"disambiguationData":[OSD([sQuery(id+"F13.wireOp",EDGE,"E27"),sQuery(id+"F13.wireOp",EDGE,"E29.1.1")])]});
            var Q8;
            Q8=makeQuery(id+"F14.opExtrude","SWEPT_EDGE",EDGE,{"disambiguationData":[OSD([sQuery(id+"F13.wireOp",EDGE,"E27"),sQuery(id+"F13.wireOp",EDGE,"E29.1.2")])]});
            var Q9;
            Q9=makeQuery(id+"F14.opExtrude","SWEPT_EDGE",EDGE,{"disambiguationData":[OSD([sQuery(id+"F13.wireOp",EDGE,"E29.1.2"),sQuery(id+"F13.wireOp",EDGE,"E37.1.8"),sQuery(id+"F13.wireOp",EDGE,"E29.1.0")])]});
            var Q10;
            Q10=makeQuery(id+"F14.opExtrude","SWEPT_EDGE",EDGE,{"disambiguationData":[OSD([sQuery(id+"F13.wireOp",EDGE,"E27"),sQuery(id+"F13.wireOp",EDGE,"E29.3.1")])]});
            var Q11;
            Q11=makeQuery(id+"F14.opExtrude","SWEPT_EDGE",EDGE,{"disambiguationData":[OSD([sQuery(id+"F13.wireOp",EDGE,"E29.3.1"),sQuery(id+"F13.wireOp",EDGE,"E37.3.8"),sQuery(id+"F13.wireOp",EDGE,"E29.3.0")])]});
            var Q12;
            Q12=makeQuery(id+"F14.opExtrude","SWEPT_EDGE",EDGE,{"disambiguationData":[OSD([sQuery(id+"F13.wireOp",EDGE,"E27"),sQuery(id+"F13.wireOp",EDGE,"E29.2.2")])]});
            var Q13;
            Q13=makeQuery(id+"F14.opExtrude","SWEPT_EDGE",EDGE,{"disambiguationData":[OSD([sQuery(id+"F13.wireOp",EDGE,"E29.2.2"),sQuery(id+"F13.wireOp",EDGE,"E37.2.8"),sQuery(id+"F13.wireOp",EDGE,"E29.2.0")])]});
            var Q14;
            Q14=makeQuery(id+"F14.opExtrude","SWEPT_EDGE",EDGE,{"disambiguationData":[OSD([sQuery(id+"F13.wireOp",EDGE,"E27"),sQuery(id+"F13.wireOp",EDGE,"E29.2.1")])]});
            var Q15;
            Q15=makeQuery(id+"F14.opExtrude","SWEPT_EDGE",EDGE,{"disambiguationData":[OSD([sQuery(id+"F13.wireOp",EDGE,"E29.2.1"),sQuery(id+"F13.wireOp",EDGE,"E37.2.8"),sQuery(id+"F13.wireOp",EDGE,"E29.2.0")])]});
            var Q16;
            Q16=makeQuery(id+"F16.boolean.opBoolean","COPY",EDGE,{"derivedFrom":makeQuery(id+"F16.opExtrude","SWEPT_EDGE",EDGE,{"disambiguationData":[OSD([sQuery(id+"F15.wireOp",EDGE,"E41.1.0"),sQuery(id+"F15.wireOp",EDGE,"E41.1.2")])]})});
            var Q17;
            Q17=makeQuery(id+"F16.boolean.opBoolean","COPY",EDGE,{"derivedFrom":makeQuery(id+"F16.opExtrude","SWEPT_EDGE",EDGE,{"disambiguationData":[OSD([sQuery(id+"F15.wireOp",EDGE,"E41.1.1"),sQuery(id+"F15.wireOp",EDGE,"E41.1.2")])]})});
            var Q18;
            Q18=makeQuery(id+"F16.boolean.opBoolean","COPY",EDGE,{"derivedFrom":makeQuery(id+"F16.opExtrude","SWEPT_EDGE",EDGE,{"disambiguationData":[OSD([sQuery(id+"F15.wireOp",EDGE,"E38"),sQuery(id+"F15.wireOp",EDGE,"E39")])]})});
            var Q19;
            Q19=makeQuery(id+"F16.boolean.opBoolean","COPY",EDGE,{"derivedFrom":makeQuery(id+"F16.opExtrude","SWEPT_EDGE",EDGE,{"disambiguationData":[OSD([sQuery(id+"F15.wireOp",EDGE,"E38"),sQuery(id+"F15.wireOp",EDGE,"E40")])]})});
            var Q20;
            Q20=makeQuery(id+"F16.boolean.opBoolean","COPY",EDGE,{"derivedFrom":makeQuery(id+"F16.opExtrude","SWEPT_EDGE",EDGE,{"disambiguationData":[OSD([sQuery(id+"F15.wireOp",EDGE,"E41.2.0"),sQuery(id+"F15.wireOp",EDGE,"E41.2.2")])]})});
            var Q21;
            Q21=makeQuery(id+"F16.boolean.opBoolean","COPY",EDGE,{"derivedFrom":makeQuery(id+"F16.opExtrude","SWEPT_EDGE",EDGE,{"disambiguationData":[OSD([sQuery(id+"F15.wireOp",EDGE,"E41.2.1"),sQuery(id+"F15.wireOp",EDGE,"E41.2.2")])]})});
            var Q22;
            Q22=makeQuery(id+"F16.boolean.opBoolean","COPY",EDGE,{"derivedFrom":makeQuery(id+"F16.opExtrude","SWEPT_EDGE",EDGE,{"disambiguationData":[OSD([sQuery(id+"F15.wireOp",EDGE,"E41.3.0"),sQuery(id+"F15.wireOp",EDGE,"E41.3.2")])]})});
            fillet(context, id + "F17", {"entities" : qUnion([Q0, Q1, Q2, Q3, Q4, Q5, Q6, Q7, Q8, Q9, Q10, Q11, Q12, Q13, Q14, Q15, Q16, Q17, Q18, Q19, Q20, Q21, Q22]), "radius" : 2.54 * mm, "tangentPropagation" : true, "allowEdgeOverflow" : false});
        }
        {
            var Q0;
            Q0=makeQuery(id+"F16.boolean.opBoolean","COPY",EDGE,{"derivedFrom":makeQuery(id+"F16.opExtrude","SWEPT_EDGE",EDGE,{"disambiguationData":[OSD([sQuery(id+"F15.wireOp",EDGE,"E41.1.0"),sQuery(id+"F15.wireOp",EDGE,"E42")])]})});
            var Q1;
            Q1=makeQuery(id+"F16.boolean.opBoolean","COPY",EDGE,{"derivedFrom":makeQuery(id+"F16.opExtrude","SWEPT_EDGE",EDGE,{"disambiguationData":[OSD([sQuery(id+"F15.wireOp",EDGE,"E41.1.1"),sQuery(id+"F15.wireOp",EDGE,"E42")])]})});
            var Q2;
            Q2=makeQuery(id+"F16.boolean.opBoolean","COPY",EDGE,{"derivedFrom":makeQuery(id+"F16.opExtrude","SWEPT_EDGE",EDGE,{"disambiguationData":[OSD([sQuery(id+"F15.wireOp",EDGE,"E39"),sQuery(id+"F15.wireOp",EDGE,"E42")])]})});
            var Q3;
            Q3=makeQuery(id+"F16.boolean.opBoolean","COPY",EDGE,{"derivedFrom":makeQuery(id+"F16.opExtrude","SWEPT_EDGE",EDGE,{"disambiguationData":[OSD([sQuery(id+"F15.wireOp",EDGE,"E40"),sQuery(id+"F15.wireOp",EDGE,"E42")])]})});
            var Q4;
            Q4=makeQuery(id+"F16.boolean.opBoolean","COPY",EDGE,{"derivedFrom":makeQuery(id+"F16.opExtrude","SWEPT_EDGE",EDGE,{"disambiguationData":[OSD([sQuery(id+"F15.wireOp",EDGE,"E41.3.1"),sQuery(id+"F15.wireOp",EDGE,"E42")])]})});
            var Q5;
            Q5=makeQuery(id+"F16.boolean.opBoolean","COPY",EDGE,{"derivedFrom":makeQuery(id+"F16.opExtrude","SWEPT_EDGE",EDGE,{"disambiguationData":[OSD([sQuery(id+"F15.wireOp",EDGE,"E41.3.0"),sQuery(id+"F15.wireOp",EDGE,"E42")])]})});
            var Q6;
            Q6=makeQuery(id+"F16.boolean.opBoolean","COPY",EDGE,{"derivedFrom":makeQuery(id+"F16.opExtrude","SWEPT_EDGE",EDGE,{"disambiguationData":[OSD([sQuery(id+"F15.wireOp",EDGE,"E41.2.0"),sQuery(id+"F15.wireOp",EDGE,"E42")])]})});
            var Q7;
            Q7=makeQuery(id+"F16.boolean.opBoolean","COPY",EDGE,{"derivedFrom":makeQuery(id+"F16.opExtrude","SWEPT_EDGE",EDGE,{"disambiguationData":[OSD([sQuery(id+"F15.wireOp",EDGE,"E41.2.1"),sQuery(id+"F15.wireOp",EDGE,"E42")])]})});
            fillet(context, id + "F18", {"entities" : qUnion([Q0, Q1, Q2, Q3, Q4, Q5, Q6, Q7]), "radius" : 1.27 * mm, "tangentPropagation" : true, "allowEdgeOverflow" : false});
        }
        {
            var Q0;
            Q0=makeQuery(id+"F14.opExtrude","CAP_FACE",FACE,{"disambiguationData":[OSD([sQuery(id+"F13.wireOp",EDGE,"E26.0"),sQuery(id+"F13.wireOp",EDGE,"E27")])],"isStart":false});
            var sketch = newSketch(context, id + "F19", { "sketchPlane" : qUnion([Q0])});
            skLineSegment(sketch, "E43.0.0", {"start": v(9.67, -51.63) * mm, "end": v(9.67, 24.57) * mm});
            skLineSegment(sketch, "E43.0.1", {"start": v(9.67, 24.57) * mm, "end": v(26.76, 24.57) * mm});
            skLineSegment(sketch, "E43.0.2", {"start": v(26.76, 24.57) * mm, "end": v(26.76, -51.63) * mm});
            skLineSegment(sketch, "E43.0.3", {"start": v(26.76, -51.63) * mm, "end": v(9.67, -51.63) * mm});
            skCircle(sketch, "E44.0", {"center": v(18.22, 18.22) * mm, "radius": 3.18 * mm});
            skSolve(sketch);
        }
        {
            var Q0;
            Q0 = qSketchRegion(id + "F19", true);
            extrude(context, id + "F20", {"entities" : qUnion([Q0]), "depth" : 6.35 * mm});
        }
        {
            var Q0;
            Q0=makeQuery(id+"F10.opExtrude","SWEPT_EDGE",EDGE,{"disambiguationData":[OSD([sQuery(id+"F9.wireOp",EDGE,"E17.bottom"),sQuery(id+"F9.wireOp",EDGE,"E17.right")])]});
            var Q1;
            Q1=makeQuery(id+"F12.opExtrude","SWEPT_EDGE",EDGE,{"disambiguationData":[OSD([sQuery(id+"F11.wireOp",EDGE,"E24.0.0"),sQuery(id+"F11.wireOp",EDGE,"E24.0.1")])]});
            var Q2;
            Q2=makeQuery(id+"F12.opExtrude","SWEPT_EDGE",EDGE,{"disambiguationData":[OSD([sQuery(id+"F11.wireOp",EDGE,"E24.0.0"),sQuery(id+"F11.wireOp",EDGE,"E24.0.3")])]});
            var Q3;
            Q3=makeQuery(id+"F10.opExtrude","SWEPT_EDGE",EDGE,{"disambiguationData":[OSD([sQuery(id+"F9.wireOp",EDGE,"E17.bottom"),sQuery(id+"F9.wireOp",EDGE,"E17.left")])]});
            var Q4;
            Q4=makeQuery(id+"F10.opExtrude","SWEPT_EDGE",EDGE,{"disambiguationData":[OSD([sQuery(id+"F9.wireOp",EDGE,"E21.bottom"),sQuery(id+"F9.wireOp",EDGE,"E21.right")])]});
            var Q5;
            Q5=makeQuery(id+"F10.opExtrude","SWEPT_EDGE",EDGE,{"disambiguationData":[OSD([sQuery(id+"F9.wireOp",EDGE,"E21.bottom"),sQuery(id+"F9.wireOp",EDGE,"E21.left")])]});
            var Q6;
            Q6=makeQuery(id+"F20.opExtrude","SWEPT_EDGE",EDGE,{"disambiguationData":[OSD([sQuery(id+"F19.wireOp",EDGE,"E43.0.0"),sQuery(id+"F19.wireOp",EDGE,"E43.0.1")])]});
            var Q7;
            Q7=makeQuery(id+"F20.opExtrude","SWEPT_EDGE",EDGE,{"disambiguationData":[OSD([sQuery(id+"F19.wireOp",EDGE,"E43.0.1"),sQuery(id+"F19.wireOp",EDGE,"E43.0.2")])]});
            fillet(context, id + "F21", {"entities" : qUnion([Q0, Q1, Q2, Q3, Q4, Q5, Q6, Q7]), "radius" : 6.35 * mm, "tangentPropagation" : true, "allowEdgeOverflow" : false});
        }
    });
